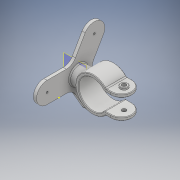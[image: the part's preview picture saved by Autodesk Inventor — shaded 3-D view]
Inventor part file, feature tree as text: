
AUTODESK INVENTOR PART (.ipt)
format: ipt  version: 2018 (Build 220112000, 112)  size: 344,576 bytes
history: native  units: mm
features: sketch x7, fillet x6, extrude x5, hole x4, plane x1
ambient origin geometry x8: Origin, YZ Plane, XZ Plane, XY Plane, X Axis, Y Axis, Z Axis, Center Point
bodies: 实体1 (feature_tree)
feature tree (23):
  extrude  "拉伸1"  Depth=20.0mm
  extrude  "拉伸2"  Depth=3.0mm TaperAngle=0.0deg
  sketch  "草图3"  dims[d0=20.0mm d3=20.0mm]
  sketch  "草图4"  dims[d4=20.0mm d6=3.0mm d7=0.0mm]
  sketch  "草图5"  dims[d9=10.0mm d10=0.0mm d27=20.0mm d28=0.0mm d29=1.0mm]
  plane  "工作平面1"
  extrude  "拉伸4"  Depth=10.0mm TaperAngle=0.0deg
  fillet  "圆角1"  Radius=1.0mm
  fillet  "圆角2"  Radius=20.594885mm
  fillet  "圆角3"  Radius=0.5mm
  hole  "孔1"  [1 undecoded]
  fillet  "圆角4"  Radius=10.0mm
  hole  "孔2"  [1 undecoded]
  hole  "孔3"  [1 undecoded]
  hole  "孔4"  [1 undecoded]
  sketch  "草图7"  dims[d40=7.421mm d41=10.0mm]
  extrude  "拉伸5"  Depth=10.0mm
  fillet  "圆角5"  Radius=1.0mm
  fillet  "圆角6"  Radius=12.0mm
  extrude  "拉伸6"  Depth=10.0mm
  sketch  "草图6"  dims[d30=10.0mm d31=7.5mm d32=4.0mm d33=6.0mm d34=4.0mm d35=2.0mm d36=90.0deg d37=0.5mm d38=20.594885mm d39=0.5mm]
  sketch  "草图8"  dims[d42=1.941mm d43=5.029mm d44=4.0mm d45=2.0mm d46=90.0deg d47=7.675mm d48=20.594885mm d49=10.0mm d50=10.0mm]
  sketch  "草图11"  dims[d51=1.941mm d52=5.029mm d53=4.0mm d54=2.0mm d55=90.0deg d56=7.675mm d57=20.594885mm d58=10.0mm d59=10.0mm d60=1.941mm d61=5.029mm d62=4.0mm d63=2.0mm d64=90.0deg d65=7.675mm d66=20.594885mm d67=7.0mm d68=2.0mm d69=0.0mm d70=0.5mm d71=2.0mm d72=1.0mm d73=0.0mm d74=12.0mm d75=12.0mm d76=12.0mm d77=2.0mm d78=0.0mm]
note: 4 required parameter values undecoded (feature->parameter linkage not recoverable at this tier; creation-order binding heuristic only, values carry confidence <= 0.55)
